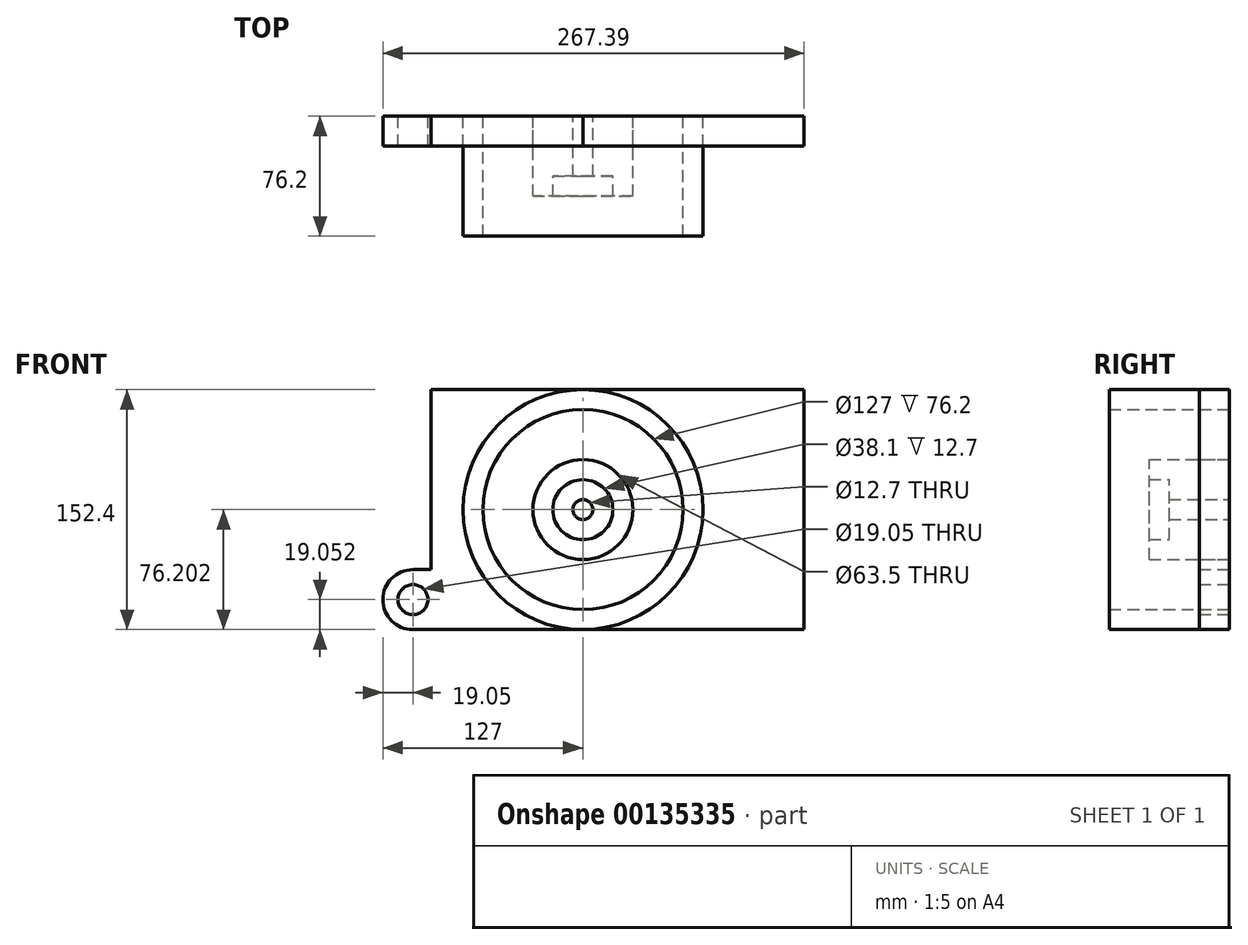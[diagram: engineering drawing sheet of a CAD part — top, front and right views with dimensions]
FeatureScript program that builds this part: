
annotation { "Feature Type Name" : "Feature", "Feature Type Description" : "" }
export const myFeature = defineFeature(function(context is Context, id is Id, definition is map)
    precondition{}
    {
        {
            var Q0;
            Q0=qCreatedBy(makeId("Front.planeOp"),FACE);
            var sketch = newSketch(context, id + "F0", { "sketchPlane" : qUnion([Q0])});
            skLineSegment(sketch, "E0", {"start": v(-96.43, -9.63) * mm, "end": v(-96.43, -162.03) * mm});
            skLineSegment(sketch, "E1", {"start": v(-96.43, -162.03) * mm, "end": v(140.39, -162.03) * mm});
            skLineSegment(sketch, "E2", {"start": v(140.39, -162.03) * mm, "end": v(140.39, -9.63) * mm});
            skCircle(sketch, "E3", {"center": v(0, -85.83) * mm, "radius": 6.35 * mm});
            skCircle(sketch, "E4", {"center": v(0, -85.83) * mm, "radius": 19.05 * mm});
            skCircle(sketch, "E5", {"center": v(0, -85.83) * mm, "radius": 31.75 * mm});
            skCircle(sketch, "E6", {"center": v(0, -85.83) * mm, "radius": 63.5 * mm});
            skCircle(sketch, "E7", {"center": v(0, -85.83) * mm, "radius": 76.2 * mm});
            skLineSegment(sketch, "E8", {"start": v(140.39, -9.63) * mm, "end": v(-96.43, -9.63) * mm});
            skArc(sketch, "E9", {"start": v(-107.95, -123.93) * mm, "mid": v(-127, -142.98) * mm, "end": v(-107.95, -162.03) * mm});
            skCircle(sketch, "E10", {"center": v(-107.95, -142.98) * mm, "radius": 9.53 * mm});
            skLineSegment(sketch, "E11", {"start": v(-107.95, -162.03) * mm, "end": v(-96.43, -162.03) * mm});
            skLineSegment(sketch, "E12", {"start": v(-107.95, -123.93) * mm, "end": v(-96.43, -123.93) * mm});
            skLineSegment(sketch, "E13", {"start": v(140.39, -123.93) * mm, "end": v(151.9, -123.93) * mm});
            skLineSegment(sketch, "E14", {"start": v(140.39, -162.03) * mm, "end": v(151.9, -162.03) * mm});
            skArc(sketch, "E15", {"start": v(151.9, -162.03) * mm, "mid": v(170.95, -142.98) * mm, "end": v(151.9, -123.93) * mm});
            skCircle(sketch, "E16", {"center": v(151.9, -142.98) * mm, "radius": 9.53 * mm});
            skLineSegment(sketch, "E17", {"start": v(-96.43, -37.63) * mm, "end": v(-112.92, -37.63) * mm});
            skLineSegment(sketch, "E18", {"start": v(-96.43, -9.63) * mm, "end": v(-112.41, -9.63) * mm});
            skArc(sketch, "E19", {"start": v(-112.41, -9.63) * mm, "mid": v(-126.41, -23.38) * mm, "end": v(-112.92, -37.63) * mm});
            skCircle(sketch, "E20", {"center": v(-112.41, -23.63) * mm, "radius": 6.65 * mm});
            skLineSegment(sketch, "E21", {"start": v(140.39, -9.63) * mm, "end": v(154.22, -9.63) * mm});
            skLineSegment(sketch, "E22", {"start": v(140.39, -30.56) * mm, "end": v(154.72, -30.56) * mm});
            skArc(sketch, "E23", {"start": v(154.72, -30.56) * mm, "mid": v(165.2, -19.83) * mm, "end": v(154.22, -9.63) * mm});
            skCircle(sketch, "E24", {"center": v(154.72, -20.09) * mm, "radius": 6.26 * mm});
            skSolve(sketch);
        }
        {
            var Q0;
            {var subQ0=sQuery(id+"F0.wireOp",EDGE,"E2");Q0=makeQuery(id+"F0.imprint","IMPRINT",FACE,{"disambiguationData":[TD([[makeQuery(id+"F0.imprint","IMPRINT",EDGE,{"derivedFrom":subQ0}),1.0]])]});}
            var Q1;
            {var subQ3=sQuery(id+"F0.wireOp",EDGE,"E8");var subQ5=sQuery(id+"F0.wireOp",EDGE,"E0");var subQ8=makeQuery(id+"F0.imprint","INTERSECT",VERTEX,{"derivedFrom":[subQ5,subQ3]});Q1=makeQuery(id+"F0.imprint","IMPRINT",FACE,{"disambiguationData":[TD([[makeQuery(id+"F0.imprint","IMPRINT",EDGE,{"disambiguationData":[TD([[subQ8,-1.0]])],"derivedFrom":subQ5}),1.0]])]});}
            var Q2;
            Q2=makeQuery(id+"F0.imprint","IMPRINT",FACE,{"disambiguationData":[TD([[makeQuery(id+"F0.imprint","IMPRINT",EDGE,{"derivedFrom":sQuery(id+"F0.wireOp",EDGE,"E9")}),1.0]])]});
            var Q3;
            Q3=makeQuery(id+"F0.imprint","IMPRINT",FACE,{"disambiguationData":[TD([[makeQuery(id+"F0.imprint","IMPRINT",EDGE,{"derivedFrom":sQuery(id+"F0.wireOp",EDGE,"E5")}),-1.0]])]});
            extrude(context, id + "F1", {"entities" : qUnion([Q0, Q1, Q2, Q3]), "depth" : 19.05 * mm});
        }
        {
            var Q0;
            Q0=makeQuery(id+"F0.imprint","IMPRINT",FACE,{"disambiguationData":[TD([[makeQuery(id+"F0.imprint","IMPRINT",EDGE,{"derivedFrom":sQuery(id+"F0.wireOp",EDGE,"E6")}),-1.0]])]});
            extrude(context, id + "F2", {"entities" : qUnion([Q0]), "depth" : 76.2 * mm});
        }
        {
            var Q0;
            Q0=makeQuery(id+"F0.imprint","IMPRINT",FACE,{"disambiguationData":[TD([[makeQuery(id+"F0.imprint","IMPRINT",EDGE,{"derivedFrom":sQuery(id+"F0.wireOp",EDGE,"E4")}),-1.0]])]});
            extrude(context, id + "F3", {"entities" : qUnion([Q0]), "depth" : 50.8 * mm});
        }
        {
            var Q0;
            Q0=makeQuery(id+"F0.imprint","IMPRINT",FACE,{"disambiguationData":[TD([[makeQuery(id+"F0.imprint","IMPRINT",EDGE,{"derivedFrom":sQuery(id+"F0.wireOp",EDGE,"E3")}),-1.0]])]});
            extrude(context, id + "F4", {"entities" : qUnion([Q0]), "operationType" : NewBodyOperationType.ADD, "depth" : 38.1 * mm});
        }
    });
